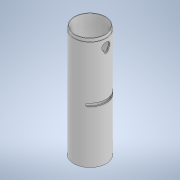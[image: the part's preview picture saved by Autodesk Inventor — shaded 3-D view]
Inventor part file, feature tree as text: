
AUTODESK INVENTOR PART (.ipt)
format: ipt  version: 2020.3 (Build 243373000, 373)  size: 191,488 bytes
history: native  units: mm
features: extrude x5, sketch x4, plane x1
ambient origin geometry x8: Origin, YZ Plane, XZ Plane, XY Plane, X Axis, Y Axis, Z Axis, Center Point
bodies: Solid1 (feature_tree)
feature tree (10):
  sketch  "Sketch1"  dims[d0=51.8mm d1=50.0mm]
  extrude  "Extrusion1"  Depth=50.0mm
  extrude  "Extrusion2"  Depth=95.0mm TaperAngle=0.0deg
  plane  "Work Plane1"
  extrude  "Extrusion3"  Depth=85.0mm TaperAngle=0.0deg
  extrude  "Extrusion4"  Depth=5.0mm
  extrude  "Extrusion5"  Depth=20.0mm
  sketch  "Sketch3"  dims[d5=180.0mm d6=0.0mm d10=85.0mm d11=0.0mm]
  sketch  "Sketch4"  dims[d12=20.0mm d13=40.0mm d14=51.8mm d15=50.0mm d16=53.6mm d17=20.0mm d18=5.0mm d19=0.0mm d20=13.0mm d21=7.0mm d22=11.5mm d23=16.0mm d24=30.0mm d25=0.0mm d26=40.0mm d27=5.0mm d28=30.0mm d29=0.0mm]
  sketch  "Sketch2"  dims[d2=53.6mm d3=95.0mm d4=0.0mm]
